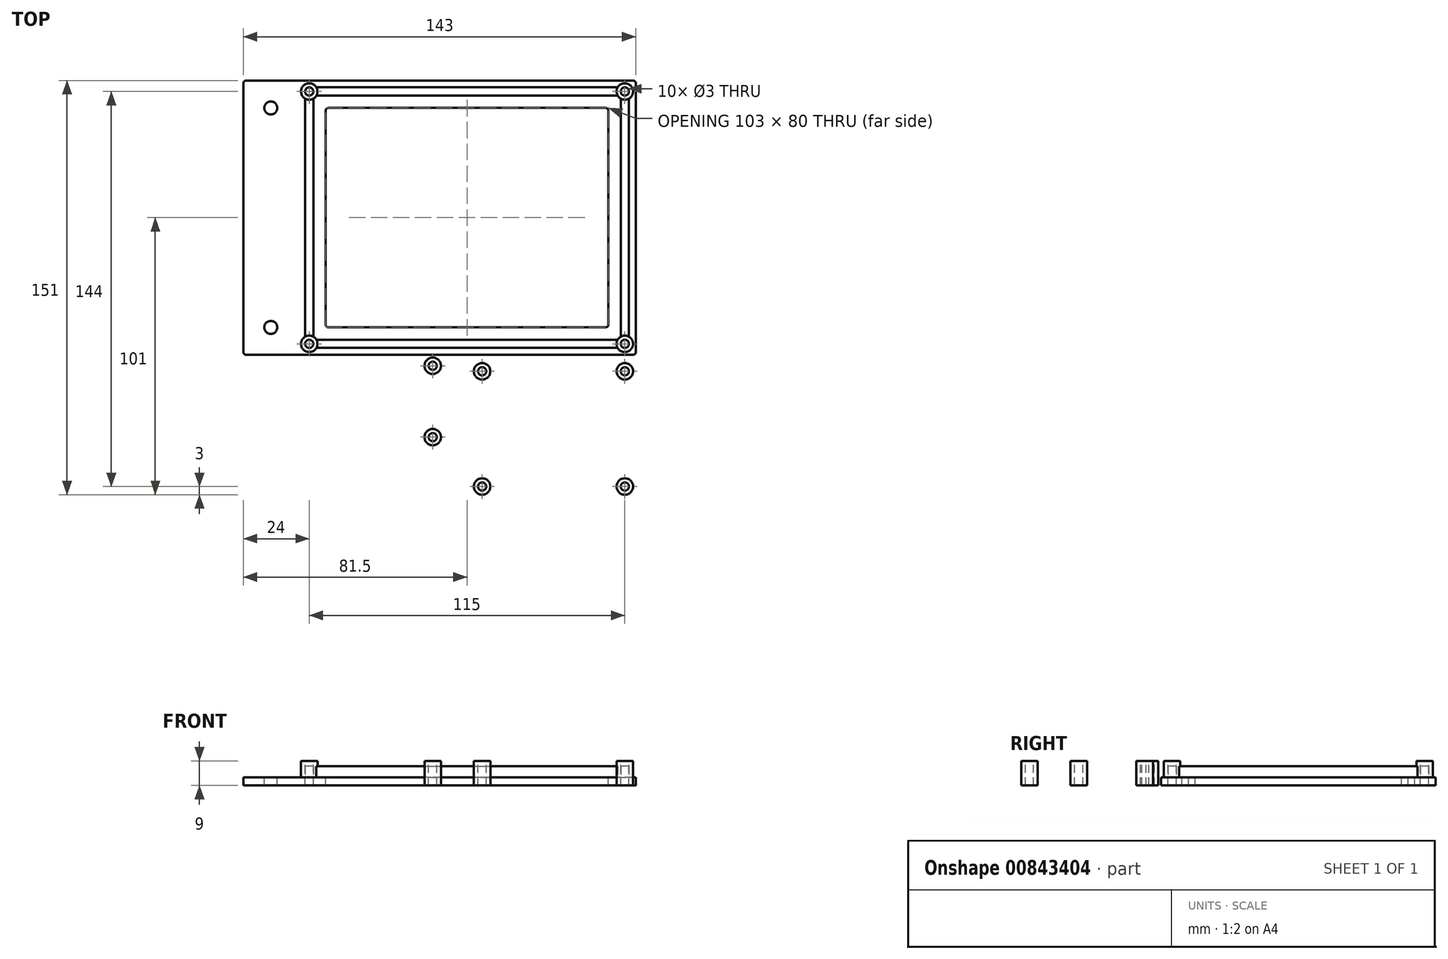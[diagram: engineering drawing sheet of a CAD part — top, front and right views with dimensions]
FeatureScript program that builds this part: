
annotation { "Feature Type Name" : "Feature", "Feature Type Description" : "" }
export const myFeature = defineFeature(function(context is Context, id is Id, definition is map)
    precondition{}
    {
        {
            var Q0;
            Q0=qCreatedBy(makeId("Top.planeOp"),FACE);
            var sketch = newSketch(context, id + "F0", { "sketchPlane" : qUnion([Q0])});
            skLineSegment(sketch, "E0.bottom", {"start": v(61.5, -50) * mm, "end": v(-61.5, -50) * mm});
            skLineSegment(sketch, "E0.top", {"start": v(61.5, 50) * mm, "end": v(-61.5, 50) * mm});
            skLineSegment(sketch, "E0.left", {"start": v(61.5, -50) * mm, "end": v(61.5, 50) * mm});
            skLineSegment(sketch, "E0.right", {"start": v(-61.5, -50) * mm, "end": v(-61.5, 50) * mm});
            skPoint(sketch, "E0.middle", {"position": v(0, 0) * mm});
            skLineSegment(sketch, "E1.bottom", {"start": v(-61.5, 50) * mm, "end": v(-81.5, 50) * mm});
            skLineSegment(sketch, "E1.top", {"start": v(-61.5, -50) * mm, "end": v(-81.5, -50) * mm});
            skLineSegment(sketch, "E1.left", {"start": v(-61.5, 50) * mm, "end": v(-61.5, -50) * mm});
            skLineSegment(sketch, "E1.right", {"start": v(-81.5, 50) * mm, "end": v(-81.5, -50) * mm});
            skCircle(sketch, "E2", {"center": v(-71.5, 40) * mm, "radius": 2.38 * mm});
            skCircle(sketch, "E3", {"center": v(-71.5, -40) * mm, "radius": 2.38 * mm});
            skCircle(sketch, "E4", {"center": v(-57.5, -46) * mm, "radius": 1.5 * mm});
            skCircle(sketch, "E5", {"center": v(57.5, -46) * mm, "radius": 1.5 * mm});
            skCircle(sketch, "E6", {"center": v(57.5, 46) * mm, "radius": 1.5 * mm});
            skCircle(sketch, "E7", {"center": v(-57.5, 46) * mm, "radius": 1.5 * mm});
            skCircle(sketch, "E8.0", {"center": v(-57.5, 46) * mm, "radius": 3 * mm});
            skCircle(sketch, "E9.0", {"center": v(57.5, 46) * mm, "radius": 3 * mm});
            skCircle(sketch, "E10.0", {"center": v(57.5, -46) * mm, "radius": 3 * mm});
            skCircle(sketch, "E11.0", {"center": v(-57.5, -46) * mm, "radius": 3 * mm});
            skLineSegment(sketch, "E12.bottom", {"start": v(51.5, -40) * mm, "end": v(-51.5, -40) * mm});
            skLineSegment(sketch, "E12.top", {"start": v(51.5, 40) * mm, "end": v(-51.5, 40) * mm});
            skLineSegment(sketch, "E12.left", {"start": v(51.5, -40) * mm, "end": v(51.5, 40) * mm});
            skLineSegment(sketch, "E12.right", {"start": v(-51.5, -40) * mm, "end": v(-51.5, 40) * mm});
            skLineSegment(sketch, "E13.bottom", {"start": v(-57.5, 44.5) * mm, "end": v(57.5, 44.5) * mm});
            skLineSegment(sketch, "E13.top", {"start": v(-57.5, 47.5) * mm, "end": v(57.5, 47.5) * mm});
            skLineSegment(sketch, "E14.bottom", {"start": v(-57.5, -47.5) * mm, "end": v(57.5, -47.5) * mm});
            skLineSegment(sketch, "E14.top", {"start": v(-57.5, -44.5) * mm, "end": v(57.5, -44.5) * mm});
            skLineSegment(sketch, "E15.left", {"start": v(59, -46) * mm, "end": v(59, 46) * mm});
            skLineSegment(sketch, "E15.right", {"start": v(56, -46) * mm, "end": v(56, 46) * mm});
            skLineSegment(sketch, "E16.left", {"start": v(-56, 46) * mm, "end": v(-56, -46) * mm});
            skLineSegment(sketch, "E16.right", {"start": v(-59, 46) * mm, "end": v(-59, -46) * mm});
            skLineSegment(sketch, "E17.bottom", {"start": v(61.5, -50) * mm, "end": v(-0.5, -50) * mm});
            skLineSegment(sketch, "E17.top", {"start": v(61.5, -102) * mm, "end": v(-0.5, -102) * mm});
            skLineSegment(sketch, "E17.left", {"start": v(61.5, -50) * mm, "end": v(61.5, -102) * mm});
            skLineSegment(sketch, "E17.right", {"start": v(-0.5, -50) * mm, "end": v(-0.5, -102) * mm});
            skCircle(sketch, "E18", {"center": v(5.5, -56) * mm, "radius": 1.5 * mm});
            skCircle(sketch, "E19", {"center": v(57.5, -56) * mm, "radius": 1.5 * mm});
            skCircle(sketch, "E20", {"center": v(57.5, -98) * mm, "radius": 1.5 * mm});
            skCircle(sketch, "E21", {"center": v(5.5, -98) * mm, "radius": 1.5 * mm});
            skCircle(sketch, "E22.0", {"center": v(5.5, -56) * mm, "radius": 3 * mm});
            skCircle(sketch, "E23.0", {"center": v(57.5, -56) * mm, "radius": 3 * mm});
            skCircle(sketch, "E24.0", {"center": v(57.5, -98) * mm, "radius": 3 * mm});
            skCircle(sketch, "E25.0", {"center": v(5.5, -98) * mm, "radius": 3 * mm});
            skLineSegment(sketch, "E26.bottom", {"start": v(-0.5, -50) * mm, "end": v(-30.5, -50) * mm});
            skLineSegment(sketch, "E26.top", {"start": v(-0.5, -84) * mm, "end": v(-30.5, -84) * mm});
            skLineSegment(sketch, "E26.left", {"start": v(-0.5, -50) * mm, "end": v(-0.5, -84) * mm});
            skLineSegment(sketch, "E26.right", {"start": v(-30.5, -50) * mm, "end": v(-30.5, -84) * mm});
            skCircle(sketch, "E27", {"center": v(-12.5, -54) * mm, "radius": 1.5 * mm});
            skCircle(sketch, "E28", {"center": v(-12.5, -80) * mm, "radius": 1.5 * mm});
            skCircle(sketch, "E29.0", {"center": v(-12.5, -54) * mm, "radius": 3 * mm});
            skCircle(sketch, "E30.0", {"center": v(-12.5, -80) * mm, "radius": 3 * mm});
            skPoint(sketch, "E31", {"position": v(31.5, -77) * mm});
            skLineSegment(sketch, "E32.bottom", {"start": v(53.5, -94) * mm, "end": v(9.5, -94) * mm});
            skLineSegment(sketch, "E32.top", {"start": v(53.5, -60) * mm, "end": v(9.5, -60) * mm});
            skLineSegment(sketch, "E32.left", {"start": v(53.5, -94) * mm, "end": v(53.5, -60) * mm});
            skLineSegment(sketch, "E32.right", {"start": v(9.5, -94) * mm, "end": v(9.5, -60) * mm});
            skSolve(sketch);
        }
        {
            var Q0;
            Q0=makeQuery(id+"F0.imprint","IMPRINT",FACE,{"disambiguationData":[TD([[makeQuery(id+"F0.imprint","IMPRINT",EDGE,{"derivedFrom":sQuery(id+"F0.wireOp",EDGE,"E0.bottom")}),-1.0]])]});
            var Q1;
            Q1=makeQuery(id+"F0.imprint","IMPRINT",FACE,{"disambiguationData":[TD([[makeQuery(id+"F0.imprint","IMPRINT",EDGE,{"derivedFrom":sQuery(id+"F0.wireOp",EDGE,"E1.bottom")}),1.0]])]});
            var Q2;
            Q2=makeQuery(id+"F0.imprint","IMPRINT",FACE,{"disambiguationData":[TD([[makeQuery(id+"F0.imprint","IMPRINT",EDGE,{"derivedFrom":sQuery(id+"F0.wireOp",EDGE,"E7")}),-1.0]])]});
            var Q3;
            Q3=makeQuery(id+"F0.imprint","IMPRINT",FACE,{"disambiguationData":[TD([[makeQuery(id+"F0.imprint","IMPRINT",EDGE,{"derivedFrom":sQuery(id+"F0.wireOp",EDGE,"E6")}),-1.0]])]});
            var Q4;
            Q4=makeQuery(id+"F0.imprint","IMPRINT",FACE,{"disambiguationData":[TD([[makeQuery(id+"F0.imprint","IMPRINT",EDGE,{"derivedFrom":sQuery(id+"F0.wireOp",EDGE,"E5")}),-1.0]])]});
            var Q5;
            Q5=makeQuery(id+"F0.imprint","IMPRINT",FACE,{"disambiguationData":[TD([[makeQuery(id+"F0.imprint","IMPRINT",EDGE,{"derivedFrom":sQuery(id+"F0.wireOp",EDGE,"E4")}),-1.0]])]});
            var Q6;
            {var subQ0=sQuery(id+"F0.wireOp",EDGE,"E13.top");var subQ1=sQuery(id+"F0.wireOp",EDGE,"E8.0");var subQ2=makeQuery(id+"F0.imprint","INTERSECT",VERTEX,{"derivedFrom":[subQ1,subQ0]});Q6=makeQuery(id+"F0.imprint","IMPRINT",FACE,{"disambiguationData":[TD([[makeQuery(id+"F0.imprint","IMPRINT",EDGE,{"disambiguationData":[TD([[subQ2,1.0]])],"derivedFrom":subQ1}),-1.0]])]});}
            var Q7;
            {var subQ0=sQuery(id+"F0.wireOp",EDGE,"E15.right");var subQ1=sQuery(id+"F0.wireOp",EDGE,"E9.0");var subQ2=makeQuery(id+"F0.imprint","INTERSECT",VERTEX,{"derivedFrom":[subQ1,subQ0]});Q7=makeQuery(id+"F0.imprint","IMPRINT",FACE,{"disambiguationData":[TD([[makeQuery(id+"F0.imprint","IMPRINT",EDGE,{"disambiguationData":[TD([[subQ2,-1.0]])],"derivedFrom":subQ1}),-1.0]])]});}
            var Q8;
            {var subQ0=sQuery(id+"F0.wireOp",EDGE,"E14.top");var subQ1=sQuery(id+"F0.wireOp",EDGE,"E10.0");var subQ2=makeQuery(id+"F0.imprint","INTERSECT",VERTEX,{"derivedFrom":[subQ1,subQ0]});Q8=makeQuery(id+"F0.imprint","IMPRINT",FACE,{"disambiguationData":[TD([[makeQuery(id+"F0.imprint","IMPRINT",EDGE,{"disambiguationData":[TD([[subQ2,-1.0]])],"derivedFrom":subQ1}),-1.0]])]});}
            var Q9;
            {var subQ0=sQuery(id+"F0.wireOp",EDGE,"E16.right");var subQ1=sQuery(id+"F0.wireOp",EDGE,"E8.0");var subQ2=makeQuery(id+"F0.imprint","INTERSECT",VERTEX,{"derivedFrom":[subQ1,subQ0]});Q9=makeQuery(id+"F0.imprint","IMPRINT",FACE,{"disambiguationData":[TD([[makeQuery(id+"F0.imprint","IMPRINT",EDGE,{"disambiguationData":[TD([[subQ2,-1.0]])],"derivedFrom":subQ1}),-1.0]])]});}
            var Q10;
            {var subQ0=sQuery(id+"F0.wireOp",EDGE,"E14.bottom");var subQ1=sQuery(id+"F0.wireOp",EDGE,"E4");var subQ2=makeQuery(id+"F0.imprint","INTERSECT",VERTEX,{"derivedFrom":[subQ1,subQ0]});Q10=makeQuery(id+"F0.imprint","IMPRINT",FACE,{"disambiguationData":[TD([[makeQuery(id+"F0.imprint","IMPRINT",EDGE,{"disambiguationData":[TD([[subQ2,1.0]])],"derivedFrom":subQ1}),-1.0]])]});}
            var Q11;
            {var subQ0=sQuery(id+"F0.wireOp",EDGE,"E14.bottom");var subQ1=sQuery(id+"F0.wireOp",EDGE,"E4");var subQ2=makeQuery(id+"F0.imprint","INTERSECT",VERTEX,{"derivedFrom":[subQ1,subQ0]});Q11=makeQuery(id+"F0.imprint","IMPRINT",FACE,{"disambiguationData":[TD([[makeQuery(id+"F0.imprint","IMPRINT",EDGE,{"disambiguationData":[TD([[subQ2,-1.0]])],"derivedFrom":subQ1}),-1.0]])]});}
            var Q12;
            {var subQ3=sQuery(id+"F0.wireOp",EDGE,"E14.top");var subQ5=sQuery(id+"F0.wireOp",EDGE,"E4");var subQ6=makeQuery(id+"F0.imprint","INTERSECT",VERTEX,{"derivedFrom":[subQ5,subQ3]});Q12=makeQuery(id+"F0.imprint","IMPRINT",FACE,{"disambiguationData":[TD([[makeQuery(id+"F0.imprint","IMPRINT",EDGE,{"disambiguationData":[TD([[subQ6,-1.0]])],"derivedFrom":subQ5}),-1.0]])]});}
            var Q13;
            {var subQ0=sQuery(id+"F0.wireOp",EDGE,"E16.left");var subQ1=sQuery(id+"F0.wireOp",EDGE,"E11.0");var subQ2=makeQuery(id+"F0.imprint","INTERSECT",VERTEX,{"derivedFrom":[subQ1,subQ0]});Q13=makeQuery(id+"F0.imprint","IMPRINT",FACE,{"disambiguationData":[TD([[makeQuery(id+"F0.imprint","IMPRINT",EDGE,{"disambiguationData":[TD([[subQ2,1.0]])],"derivedFrom":subQ1}),1.0]])]});}
            var Q14;
            {var subQ5=sQuery(id+"F0.wireOp",EDGE,"E14.bottom");var subQ6=sQuery(id+"F0.wireOp",EDGE,"E5");var subQ7=makeQuery(id+"F0.imprint","INTERSECT",VERTEX,{"derivedFrom":[subQ6,subQ5]});Q14=makeQuery(id+"F0.imprint","IMPRINT",FACE,{"disambiguationData":[TD([[makeQuery(id+"F0.imprint","IMPRINT",EDGE,{"disambiguationData":[TD([[subQ7,1.0]])],"derivedFrom":subQ6}),-1.0]])]});}
            var Q15;
            {var subQ1=sQuery(id+"F0.wireOp",EDGE,"E5");var subQ5=sQuery(id+"F0.wireOp",EDGE,"E14.top");var subQ6=makeQuery(id+"F0.imprint","INTERSECT",VERTEX,{"derivedFrom":[subQ1,subQ5]});Q15=makeQuery(id+"F0.imprint","IMPRINT",FACE,{"disambiguationData":[TD([[makeQuery(id+"F0.imprint","IMPRINT",EDGE,{"disambiguationData":[TD([[subQ6,1.0]])],"derivedFrom":subQ1}),-1.0]])]});}
            var Q16;
            {var subQ0=sQuery(id+"F0.wireOp",EDGE,"E14.bottom");var subQ1=sQuery(id+"F0.wireOp",EDGE,"E5");var subQ2=makeQuery(id+"F0.imprint","INTERSECT",VERTEX,{"derivedFrom":[subQ1,subQ0]});Q16=makeQuery(id+"F0.imprint","IMPRINT",FACE,{"disambiguationData":[TD([[makeQuery(id+"F0.imprint","IMPRINT",EDGE,{"disambiguationData":[TD([[subQ2,-1.0]])],"derivedFrom":subQ1}),-1.0]])]});}
            var Q17;
            {var subQ0=sQuery(id+"F0.wireOp",EDGE,"E15.right");var subQ1=sQuery(id+"F0.wireOp",EDGE,"E10.0");var subQ2=makeQuery(id+"F0.imprint","INTERSECT",VERTEX,{"derivedFrom":[subQ1,subQ0]});Q17=makeQuery(id+"F0.imprint","IMPRINT",FACE,{"disambiguationData":[TD([[makeQuery(id+"F0.imprint","IMPRINT",EDGE,{"disambiguationData":[TD([[subQ2,-1.0]])],"derivedFrom":subQ1}),1.0]])]});}
            var Q18;
            {var subQ0=sQuery(id+"F0.wireOp",EDGE,"E13.top");var subQ1=sQuery(id+"F0.wireOp",EDGE,"E6");var subQ2=makeQuery(id+"F0.imprint","INTERSECT",VERTEX,{"derivedFrom":[subQ1,subQ0]});Q18=makeQuery(id+"F0.imprint","IMPRINT",FACE,{"disambiguationData":[TD([[makeQuery(id+"F0.imprint","IMPRINT",EDGE,{"disambiguationData":[TD([[subQ2,1.0]])],"derivedFrom":subQ1}),-1.0]])]});}
            var Q19;
            {var subQ1=sQuery(id+"F0.wireOp",EDGE,"E6");var subQ5=sQuery(id+"F0.wireOp",EDGE,"E13.bottom");var subQ6=makeQuery(id+"F0.imprint","INTERSECT",VERTEX,{"derivedFrom":[subQ1,subQ5]});Q19=makeQuery(id+"F0.imprint","IMPRINT",FACE,{"disambiguationData":[TD([[makeQuery(id+"F0.imprint","IMPRINT",EDGE,{"disambiguationData":[TD([[subQ6,-1.0]])],"derivedFrom":subQ1}),-1.0]])]});}
            var Q20;
            {var subQ0=sQuery(id+"F0.wireOp",EDGE,"E13.top");var subQ1=sQuery(id+"F0.wireOp",EDGE,"E6");var subQ2=makeQuery(id+"F0.imprint","INTERSECT",VERTEX,{"derivedFrom":[subQ1,subQ0]});Q20=makeQuery(id+"F0.imprint","IMPRINT",FACE,{"disambiguationData":[TD([[makeQuery(id+"F0.imprint","IMPRINT",EDGE,{"disambiguationData":[TD([[subQ2,-1.0]])],"derivedFrom":subQ1}),-1.0]])]});}
            var Q21;
            Q21=makeQuery(id+"F0.imprint","IMPRINT",FACE,{"disambiguationData":[TD([[makeQuery(id+"F0.imprint","IMPRINT",EDGE,{"derivedFrom":sQuery(id+"F0.wireOp",EDGE,"E12.bottom")}),1.0]])]});
            var Q22;
            {var subQ0=sQuery(id+"F0.wireOp",EDGE,"E13.bottom");var subQ1=sQuery(id+"F0.wireOp",EDGE,"E9.0");var subQ2=makeQuery(id+"F0.imprint","INTERSECT",VERTEX,{"derivedFrom":[subQ1,subQ0]});Q22=makeQuery(id+"F0.imprint","IMPRINT",FACE,{"disambiguationData":[TD([[makeQuery(id+"F0.imprint","IMPRINT",EDGE,{"disambiguationData":[TD([[subQ2,-1.0]])],"derivedFrom":subQ1}),1.0]])]});}
            var Q23;
            {var subQ0=sQuery(id+"F0.wireOp",EDGE,"E13.top");var subQ1=sQuery(id+"F0.wireOp",EDGE,"E7");var subQ2=makeQuery(id+"F0.imprint","INTERSECT",VERTEX,{"derivedFrom":[subQ1,subQ0]});Q23=makeQuery(id+"F0.imprint","IMPRINT",FACE,{"disambiguationData":[TD([[makeQuery(id+"F0.imprint","IMPRINT",EDGE,{"disambiguationData":[TD([[subQ2,1.0]])],"derivedFrom":subQ1}),-1.0]])]});}
            var Q24;
            {var subQ0=sQuery(id+"F0.wireOp",EDGE,"E13.top");var subQ1=sQuery(id+"F0.wireOp",EDGE,"E7");var subQ2=makeQuery(id+"F0.imprint","INTERSECT",VERTEX,{"derivedFrom":[subQ1,subQ0]});Q24=makeQuery(id+"F0.imprint","IMPRINT",FACE,{"disambiguationData":[TD([[makeQuery(id+"F0.imprint","IMPRINT",EDGE,{"disambiguationData":[TD([[subQ2,-1.0]])],"derivedFrom":subQ1}),-1.0]])]});}
            var Q25;
            {var subQ3=sQuery(id+"F0.wireOp",EDGE,"E13.bottom");var subQ7=sQuery(id+"F0.wireOp",EDGE,"E7");var subQ8=makeQuery(id+"F0.imprint","INTERSECT",VERTEX,{"derivedFrom":[subQ7,subQ3]});Q25=makeQuery(id+"F0.imprint","IMPRINT",FACE,{"disambiguationData":[TD([[makeQuery(id+"F0.imprint","IMPRINT",EDGE,{"disambiguationData":[TD([[subQ8,1.0]])],"derivedFrom":subQ7}),-1.0]])]});}
            var Q26;
            {var subQ0=sQuery(id+"F0.wireOp",EDGE,"E16.left");var subQ1=sQuery(id+"F0.wireOp",EDGE,"E8.0");var subQ2=makeQuery(id+"F0.imprint","INTERSECT",VERTEX,{"derivedFrom":[subQ1,subQ0]});Q26=makeQuery(id+"F0.imprint","IMPRINT",FACE,{"disambiguationData":[TD([[makeQuery(id+"F0.imprint","IMPRINT",EDGE,{"disambiguationData":[TD([[subQ2,-1.0]])],"derivedFrom":subQ1}),1.0]])]});}
            var Q27;
            Q27=makeQuery(id+"F0.imprint","IMPRINT",FACE,{"disambiguationData":[TD([[makeQuery(id+"F0.imprint","IMPRINT",EDGE,{"derivedFrom":sQuery(id+"F0.wireOp",EDGE,"E26.bottom")}),1.0]])]});
            var Q28;
            Q28=makeQuery(id+"F0.imprint","IMPRINT",FACE,{"disambiguationData":[TD([[makeQuery(id+"F0.imprint","IMPRINT",EDGE,{"derivedFrom":sQuery(id+"F0.wireOp",EDGE,"E17.bottom")}),1.0]])]});
            var Q29;
            Q29=makeQuery(id+"F0.imprint","IMPRINT",FACE,{"disambiguationData":[TD([[makeQuery(id+"F0.imprint","IMPRINT",EDGE,{"derivedFrom":sQuery(id+"F0.wireOp",EDGE,"E18")}),-1.0]])]});
            var Q30;
            Q30=makeQuery(id+"F0.imprint","IMPRINT",FACE,{"disambiguationData":[TD([[makeQuery(id+"F0.imprint","IMPRINT",EDGE,{"derivedFrom":sQuery(id+"F0.wireOp",EDGE,"E27")}),-1.0]])]});
            var Q31;
            Q31=makeQuery(id+"F0.imprint","IMPRINT",FACE,{"disambiguationData":[TD([[makeQuery(id+"F0.imprint","IMPRINT",EDGE,{"derivedFrom":sQuery(id+"F0.wireOp",EDGE,"E28")}),-1.0]])]});
            var Q32;
            Q32=makeQuery(id+"F0.imprint","IMPRINT",FACE,{"disambiguationData":[TD([[makeQuery(id+"F0.imprint","IMPRINT",EDGE,{"derivedFrom":sQuery(id+"F0.wireOp",EDGE,"E21")}),-1.0]])]});
            var Q33;
            Q33=makeQuery(id+"F0.imprint","IMPRINT",FACE,{"disambiguationData":[TD([[makeQuery(id+"F0.imprint","IMPRINT",EDGE,{"derivedFrom":sQuery(id+"F0.wireOp",EDGE,"E20")}),-1.0]])]});
            var Q34;
            Q34=makeQuery(id+"F0.imprint","IMPRINT",FACE,{"disambiguationData":[TD([[makeQuery(id+"F0.imprint","IMPRINT",EDGE,{"derivedFrom":sQuery(id+"F0.wireOp",EDGE,"E19")}),-1.0]])]});
            extrude(context, id + "F1", {"entities" : qUnion([Q0, Q1, Q2, Q3, Q4, Q5, Q6, Q7, Q8, Q9, Q10, Q11, Q12, Q13, Q14, Q15, Q16, Q17, Q18, Q19, Q20, Q21, Q22, Q23, Q24, Q25, Q26, Q27, Q28, Q29, Q30, Q31, Q32, Q33, Q34]), "oppositeDirection" : true, "depth" : 3 * mm, "offsetDistance" : 25 * mm});
        }
        {
            var Q0;
            Q0=makeQuery(id+"F0.imprint","IMPRINT",FACE,{"disambiguationData":[TD([[makeQuery(id+"F0.imprint","IMPRINT",EDGE,{"derivedFrom":sQuery(id+"F0.wireOp",EDGE,"E7")}),-1.0]])]});
            var Q1;
            Q1=makeQuery(id+"F0.imprint","IMPRINT",FACE,{"disambiguationData":[TD([[makeQuery(id+"F0.imprint","IMPRINT",EDGE,{"derivedFrom":sQuery(id+"F0.wireOp",EDGE,"E6")}),-1.0]])]});
            var Q2;
            Q2=makeQuery(id+"F0.imprint","IMPRINT",FACE,{"disambiguationData":[TD([[makeQuery(id+"F0.imprint","IMPRINT",EDGE,{"derivedFrom":sQuery(id+"F0.wireOp",EDGE,"E5")}),-1.0]])]});
            var Q3;
            Q3=makeQuery(id+"F0.imprint","IMPRINT",FACE,{"disambiguationData":[TD([[makeQuery(id+"F0.imprint","IMPRINT",EDGE,{"derivedFrom":sQuery(id+"F0.wireOp",EDGE,"E4")}),-1.0]])]});
            var Q4;
            {var subQ0=sQuery(id+"F0.wireOp",EDGE,"E13.top");var subQ1=sQuery(id+"F0.wireOp",EDGE,"E7");var subQ2=makeQuery(id+"F0.imprint","INTERSECT",VERTEX,{"derivedFrom":[subQ1,subQ0]});Q4=makeQuery(id+"F0.imprint","IMPRINT",FACE,{"disambiguationData":[TD([[makeQuery(id+"F0.imprint","IMPRINT",EDGE,{"disambiguationData":[TD([[subQ2,-1.0]])],"derivedFrom":subQ1}),-1.0]])]});}
            var Q5;
            {var subQ0=sQuery(id+"F0.wireOp",EDGE,"E13.top");var subQ1=sQuery(id+"F0.wireOp",EDGE,"E7");var subQ2=makeQuery(id+"F0.imprint","INTERSECT",VERTEX,{"derivedFrom":[subQ1,subQ0]});Q5=makeQuery(id+"F0.imprint","IMPRINT",FACE,{"disambiguationData":[TD([[makeQuery(id+"F0.imprint","IMPRINT",EDGE,{"disambiguationData":[TD([[subQ2,1.0]])],"derivedFrom":subQ1}),-1.0]])]});}
            var Q6;
            {var subQ3=sQuery(id+"F0.wireOp",EDGE,"E13.bottom");var subQ7=sQuery(id+"F0.wireOp",EDGE,"E7");var subQ8=makeQuery(id+"F0.imprint","INTERSECT",VERTEX,{"derivedFrom":[subQ7,subQ3]});Q6=makeQuery(id+"F0.imprint","IMPRINT",FACE,{"disambiguationData":[TD([[makeQuery(id+"F0.imprint","IMPRINT",EDGE,{"disambiguationData":[TD([[subQ8,1.0]])],"derivedFrom":subQ7}),-1.0]])]});}
            var Q7;
            {var subQ0=sQuery(id+"F0.wireOp",EDGE,"E16.left");var subQ1=sQuery(id+"F0.wireOp",EDGE,"E8.0");var subQ2=makeQuery(id+"F0.imprint","INTERSECT",VERTEX,{"derivedFrom":[subQ1,subQ0]});Q7=makeQuery(id+"F0.imprint","IMPRINT",FACE,{"disambiguationData":[TD([[makeQuery(id+"F0.imprint","IMPRINT",EDGE,{"disambiguationData":[TD([[subQ2,-1.0]])],"derivedFrom":subQ1}),1.0]])]});}
            var Q8;
            {var subQ0=sQuery(id+"F0.wireOp",EDGE,"E13.top");var subQ1=sQuery(id+"F0.wireOp",EDGE,"E6");var subQ2=makeQuery(id+"F0.imprint","INTERSECT",VERTEX,{"derivedFrom":[subQ1,subQ0]});Q8=makeQuery(id+"F0.imprint","IMPRINT",FACE,{"disambiguationData":[TD([[makeQuery(id+"F0.imprint","IMPRINT",EDGE,{"disambiguationData":[TD([[subQ2,1.0]])],"derivedFrom":subQ1}),-1.0]])]});}
            var Q9;
            {var subQ1=sQuery(id+"F0.wireOp",EDGE,"E6");var subQ5=sQuery(id+"F0.wireOp",EDGE,"E13.bottom");var subQ6=makeQuery(id+"F0.imprint","INTERSECT",VERTEX,{"derivedFrom":[subQ1,subQ5]});Q9=makeQuery(id+"F0.imprint","IMPRINT",FACE,{"disambiguationData":[TD([[makeQuery(id+"F0.imprint","IMPRINT",EDGE,{"disambiguationData":[TD([[subQ6,-1.0]])],"derivedFrom":subQ1}),-1.0]])]});}
            var Q10;
            {var subQ0=sQuery(id+"F0.wireOp",EDGE,"E13.top");var subQ1=sQuery(id+"F0.wireOp",EDGE,"E6");var subQ2=makeQuery(id+"F0.imprint","INTERSECT",VERTEX,{"derivedFrom":[subQ1,subQ0]});Q10=makeQuery(id+"F0.imprint","IMPRINT",FACE,{"disambiguationData":[TD([[makeQuery(id+"F0.imprint","IMPRINT",EDGE,{"disambiguationData":[TD([[subQ2,-1.0]])],"derivedFrom":subQ1}),-1.0]])]});}
            var Q11;
            {var subQ0=sQuery(id+"F0.wireOp",EDGE,"E13.bottom");var subQ1=sQuery(id+"F0.wireOp",EDGE,"E9.0");var subQ2=makeQuery(id+"F0.imprint","INTERSECT",VERTEX,{"derivedFrom":[subQ1,subQ0]});Q11=makeQuery(id+"F0.imprint","IMPRINT",FACE,{"disambiguationData":[TD([[makeQuery(id+"F0.imprint","IMPRINT",EDGE,{"disambiguationData":[TD([[subQ2,-1.0]])],"derivedFrom":subQ1}),1.0]])]});}
            var Q12;
            {var subQ0=sQuery(id+"F0.wireOp",EDGE,"E14.bottom");var subQ1=sQuery(id+"F0.wireOp",EDGE,"E5");var subQ2=makeQuery(id+"F0.imprint","INTERSECT",VERTEX,{"derivedFrom":[subQ1,subQ0]});Q12=makeQuery(id+"F0.imprint","IMPRINT",FACE,{"disambiguationData":[TD([[makeQuery(id+"F0.imprint","IMPRINT",EDGE,{"disambiguationData":[TD([[subQ2,-1.0]])],"derivedFrom":subQ1}),-1.0]])]});}
            var Q13;
            {var subQ1=sQuery(id+"F0.wireOp",EDGE,"E5");var subQ5=sQuery(id+"F0.wireOp",EDGE,"E14.top");var subQ6=makeQuery(id+"F0.imprint","INTERSECT",VERTEX,{"derivedFrom":[subQ1,subQ5]});Q13=makeQuery(id+"F0.imprint","IMPRINT",FACE,{"disambiguationData":[TD([[makeQuery(id+"F0.imprint","IMPRINT",EDGE,{"disambiguationData":[TD([[subQ6,1.0]])],"derivedFrom":subQ1}),-1.0]])]});}
            var Q14;
            {var subQ5=sQuery(id+"F0.wireOp",EDGE,"E14.bottom");var subQ6=sQuery(id+"F0.wireOp",EDGE,"E5");var subQ7=makeQuery(id+"F0.imprint","INTERSECT",VERTEX,{"derivedFrom":[subQ6,subQ5]});Q14=makeQuery(id+"F0.imprint","IMPRINT",FACE,{"disambiguationData":[TD([[makeQuery(id+"F0.imprint","IMPRINT",EDGE,{"disambiguationData":[TD([[subQ7,1.0]])],"derivedFrom":subQ6}),-1.0]])]});}
            var Q15;
            {var subQ0=sQuery(id+"F0.wireOp",EDGE,"E15.right");var subQ1=sQuery(id+"F0.wireOp",EDGE,"E10.0");var subQ2=makeQuery(id+"F0.imprint","INTERSECT",VERTEX,{"derivedFrom":[subQ1,subQ0]});Q15=makeQuery(id+"F0.imprint","IMPRINT",FACE,{"disambiguationData":[TD([[makeQuery(id+"F0.imprint","IMPRINT",EDGE,{"disambiguationData":[TD([[subQ2,-1.0]])],"derivedFrom":subQ1}),1.0]])]});}
            var Q16;
            {var subQ0=sQuery(id+"F0.wireOp",EDGE,"E14.bottom");var subQ1=sQuery(id+"F0.wireOp",EDGE,"E4");var subQ2=makeQuery(id+"F0.imprint","INTERSECT",VERTEX,{"derivedFrom":[subQ1,subQ0]});Q16=makeQuery(id+"F0.imprint","IMPRINT",FACE,{"disambiguationData":[TD([[makeQuery(id+"F0.imprint","IMPRINT",EDGE,{"disambiguationData":[TD([[subQ2,-1.0]])],"derivedFrom":subQ1}),-1.0]])]});}
            var Q17;
            {var subQ0=sQuery(id+"F0.wireOp",EDGE,"E14.bottom");var subQ1=sQuery(id+"F0.wireOp",EDGE,"E4");var subQ2=makeQuery(id+"F0.imprint","INTERSECT",VERTEX,{"derivedFrom":[subQ1,subQ0]});Q17=makeQuery(id+"F0.imprint","IMPRINT",FACE,{"disambiguationData":[TD([[makeQuery(id+"F0.imprint","IMPRINT",EDGE,{"disambiguationData":[TD([[subQ2,1.0]])],"derivedFrom":subQ1}),-1.0]])]});}
            var Q18;
            {var subQ3=sQuery(id+"F0.wireOp",EDGE,"E14.top");var subQ5=sQuery(id+"F0.wireOp",EDGE,"E4");var subQ6=makeQuery(id+"F0.imprint","INTERSECT",VERTEX,{"derivedFrom":[subQ5,subQ3]});Q18=makeQuery(id+"F0.imprint","IMPRINT",FACE,{"disambiguationData":[TD([[makeQuery(id+"F0.imprint","IMPRINT",EDGE,{"disambiguationData":[TD([[subQ6,-1.0]])],"derivedFrom":subQ5}),-1.0]])]});}
            var Q19;
            {var subQ0=sQuery(id+"F0.wireOp",EDGE,"E16.left");var subQ1=sQuery(id+"F0.wireOp",EDGE,"E11.0");var subQ2=makeQuery(id+"F0.imprint","INTERSECT",VERTEX,{"derivedFrom":[subQ1,subQ0]});Q19=makeQuery(id+"F0.imprint","IMPRINT",FACE,{"disambiguationData":[TD([[makeQuery(id+"F0.imprint","IMPRINT",EDGE,{"disambiguationData":[TD([[subQ2,1.0]])],"derivedFrom":subQ1}),1.0]])]});}
            var Q20;
            Q20=makeQuery(id+"F0.imprint","IMPRINT",FACE,{"disambiguationData":[TD([[makeQuery(id+"F0.imprint","IMPRINT",EDGE,{"derivedFrom":sQuery(id+"F0.wireOp",EDGE,"E27")}),-1.0]])]});
            var Q21;
            Q21=makeQuery(id+"F0.imprint","IMPRINT",FACE,{"disambiguationData":[TD([[makeQuery(id+"F0.imprint","IMPRINT",EDGE,{"derivedFrom":sQuery(id+"F0.wireOp",EDGE,"E28")}),-1.0]])]});
            var Q22;
            Q22=makeQuery(id+"F0.imprint","IMPRINT",FACE,{"disambiguationData":[TD([[makeQuery(id+"F0.imprint","IMPRINT",EDGE,{"derivedFrom":sQuery(id+"F0.wireOp",EDGE,"E18")}),-1.0]])]});
            var Q23;
            Q23=makeQuery(id+"F0.imprint","IMPRINT",FACE,{"disambiguationData":[TD([[makeQuery(id+"F0.imprint","IMPRINT",EDGE,{"derivedFrom":sQuery(id+"F0.wireOp",EDGE,"E19")}),-1.0]])]});
            var Q24;
            Q24=makeQuery(id+"F0.imprint","IMPRINT",FACE,{"disambiguationData":[TD([[makeQuery(id+"F0.imprint","IMPRINT",EDGE,{"derivedFrom":sQuery(id+"F0.wireOp",EDGE,"E20")}),-1.0]])]});
            var Q25;
            Q25=makeQuery(id+"F0.imprint","IMPRINT",FACE,{"disambiguationData":[TD([[makeQuery(id+"F0.imprint","IMPRINT",EDGE,{"derivedFrom":sQuery(id+"F0.wireOp",EDGE,"E21")}),-1.0]])]});
            extrude(context, id + "F2", {"entities" : qUnion([Q0, Q1, Q2, Q3, Q4, Q5, Q6, Q7, Q8, Q9, Q10, Q11, Q12, Q13, Q14, Q15, Q16, Q17, Q18, Q19, Q20, Q21, Q22, Q23, Q24, Q25]), "operationType" : NewBodyOperationType.ADD, "depth" : 6 * mm, "offsetDistance" : 25 * mm});
        }
        {
            var Q0;
            {var subQ0=sQuery(id+"F0.wireOp",EDGE,"E13.top");var subQ1=sQuery(id+"F0.wireOp",EDGE,"E8.0");var subQ2=makeQuery(id+"F0.imprint","INTERSECT",VERTEX,{"derivedFrom":[subQ1,subQ0]});Q0=makeQuery(id+"F0.imprint","IMPRINT",FACE,{"disambiguationData":[TD([[makeQuery(id+"F0.imprint","IMPRINT",EDGE,{"disambiguationData":[TD([[subQ2,1.0]])],"derivedFrom":subQ1}),-1.0]])]});}
            var Q1;
            {var subQ0=sQuery(id+"F0.wireOp",EDGE,"E16.right");var subQ1=sQuery(id+"F0.wireOp",EDGE,"E8.0");var subQ2=makeQuery(id+"F0.imprint","INTERSECT",VERTEX,{"derivedFrom":[subQ1,subQ0]});Q1=makeQuery(id+"F0.imprint","IMPRINT",FACE,{"disambiguationData":[TD([[makeQuery(id+"F0.imprint","IMPRINT",EDGE,{"disambiguationData":[TD([[subQ2,-1.0]])],"derivedFrom":subQ1}),-1.0]])]});}
            var Q2;
            {var subQ0=sQuery(id+"F0.wireOp",EDGE,"E14.top");var subQ1=sQuery(id+"F0.wireOp",EDGE,"E10.0");var subQ2=makeQuery(id+"F0.imprint","INTERSECT",VERTEX,{"derivedFrom":[subQ1,subQ0]});Q2=makeQuery(id+"F0.imprint","IMPRINT",FACE,{"disambiguationData":[TD([[makeQuery(id+"F0.imprint","IMPRINT",EDGE,{"disambiguationData":[TD([[subQ2,-1.0]])],"derivedFrom":subQ1}),-1.0]])]});}
            var Q3;
            {var subQ0=sQuery(id+"F0.wireOp",EDGE,"E15.right");var subQ1=sQuery(id+"F0.wireOp",EDGE,"E9.0");var subQ2=makeQuery(id+"F0.imprint","INTERSECT",VERTEX,{"derivedFrom":[subQ1,subQ0]});Q3=makeQuery(id+"F0.imprint","IMPRINT",FACE,{"disambiguationData":[TD([[makeQuery(id+"F0.imprint","IMPRINT",EDGE,{"disambiguationData":[TD([[subQ2,-1.0]])],"derivedFrom":subQ1}),-1.0]])]});}
            extrude(context, id + "F3", {"entities" : qUnion([Q0, Q1, Q2, Q3]), "operationType" : NewBodyOperationType.ADD, "depth" : 4 * mm, "offsetDistance" : 25 * mm});
        }
        {
            var Q0;
            Q0=makeQuery(id+"F1.opExtrude","SWEPT_EDGE",EDGE,{"disambiguationData":[OSD([sQuery(id+"F0.wireOp",EDGE,"E1.bottom"),sQuery(id+"F0.wireOp",EDGE,"E1.right")])]});
            var Q1;
            Q1=makeQuery(id+"F1.opExtrude","SWEPT_EDGE",EDGE,{"disambiguationData":[OSD([sQuery(id+"F0.wireOp",EDGE,"E1.top"),sQuery(id+"F0.wireOp",EDGE,"E1.right")])]});
            var Q2;
            Q2=makeQuery(id+"F1.opExtrude","SWEPT_EDGE",EDGE,{"disambiguationData":[OSD([sQuery(id+"F0.wireOp",EDGE,"E0.top"),sQuery(id+"F0.wireOp",EDGE,"E0.left")])]});
            var Q3;
            Q3=makeQuery(id+"F1.opExtrude","SWEPT_EDGE",EDGE,{"disambiguationData":[OSD([sQuery(id+"F0.wireOp",EDGE,"E0.bottom"),sQuery(id+"F0.wireOp",EDGE,"E0.left")])]});
            var Q4;
            Q4=makeQuery(id+"F1.opExtrude","SWEPT_EDGE",EDGE,{"disambiguationData":[OSD([sQuery(id+"F0.wireOp",EDGE,"E12.top"),sQuery(id+"F0.wireOp",EDGE,"E12.left")])]});
            var Q5;
            Q5=makeQuery(id+"F1.opExtrude","SWEPT_EDGE",EDGE,{"disambiguationData":[OSD([sQuery(id+"F0.wireOp",EDGE,"E12.bottom"),sQuery(id+"F0.wireOp",EDGE,"E12.left")])]});
            var Q6;
            Q6=makeQuery(id+"F1.opExtrude","SWEPT_EDGE",EDGE,{"disambiguationData":[OSD([sQuery(id+"F0.wireOp",EDGE,"E12.top"),sQuery(id+"F0.wireOp",EDGE,"E12.right")])]});
            var Q7;
            Q7=makeQuery(id+"F1.opExtrude","SWEPT_EDGE",EDGE,{"disambiguationData":[OSD([sQuery(id+"F0.wireOp",EDGE,"E12.bottom"),sQuery(id+"F0.wireOp",EDGE,"E12.right")])]});
            var Q8;
            Q8=makeQuery(id+"F1.opExtrude","SWEPT_EDGE",EDGE,{"disambiguationData":[OSD([sQuery(id+"F0.wireOp",EDGE,"E17.top"),sQuery(id+"F0.wireOp",EDGE,"E17.left")])]});
            var Q9;
            Q9=makeQuery(id+"F1.opExtrude","SWEPT_EDGE",EDGE,{"disambiguationData":[OSD([sQuery(id+"F0.wireOp",EDGE,"E17.top"),sQuery(id+"F0.wireOp",EDGE,"E17.right")])]});
            var Q10;
            Q10=makeQuery(id+"F1.opExtrude","SWEPT_EDGE",EDGE,{"disambiguationData":[OSD([sQuery(id+"F0.wireOp",EDGE,"E26.top"),sQuery(id+"F0.wireOp",EDGE,"E26.right")])]});
            var Q11;
            Q11=makeQuery(id+"F1.opExtrude","SWEPT_EDGE",EDGE,{"disambiguationData":[OSD([sQuery(id+"F0.wireOp",EDGE,"E32.top"),sQuery(id+"F0.wireOp",EDGE,"E32.right")])]});
            var Q12;
            Q12=makeQuery(id+"F1.opExtrude","SWEPT_EDGE",EDGE,{"disambiguationData":[OSD([sQuery(id+"F0.wireOp",EDGE,"E32.top"),sQuery(id+"F0.wireOp",EDGE,"E32.left")])]});
            var Q13;
            Q13=makeQuery(id+"F1.opExtrude","SWEPT_EDGE",EDGE,{"disambiguationData":[OSD([sQuery(id+"F0.wireOp",EDGE,"E17.right"),sQuery(id+"F0.wireOp",EDGE,"E26.top"),sQuery(id+"F0.wireOp",EDGE,"E26.left")])]});
            var Q14;
            Q14=makeQuery(id+"F1.opExtrude","SWEPT_EDGE",EDGE,{"disambiguationData":[OSD([sQuery(id+"F0.wireOp",EDGE,"E0.bottom"),sQuery(id+"F0.wireOp",EDGE,"E26.bottom"),sQuery(id+"F0.wireOp",EDGE,"E26.right")])]});
            var Q15;
            Q15=makeQuery(id+"F1.opExtrude","SWEPT_EDGE",EDGE,{"disambiguationData":[OSD([sQuery(id+"F0.wireOp",EDGE,"E32.bottom"),sQuery(id+"F0.wireOp",EDGE,"E32.left")])]});
            var Q16;
            Q16=makeQuery(id+"F1.opExtrude","SWEPT_EDGE",EDGE,{"disambiguationData":[OSD([sQuery(id+"F0.wireOp",EDGE,"E32.bottom"),sQuery(id+"F0.wireOp",EDGE,"E32.right")])]});
            fillet(context, id + "F4", {"entities" : qUnion([Q0, Q1, Q2, Q3, Q4, Q5, Q6, Q7, Q8, Q9, Q10, Q11, Q12, Q13, Q14, Q15, Q16]), "radius" : 1 * mm, "tangentPropagation" : true, "allowEdgeOverflow" : false});
        }
    });
